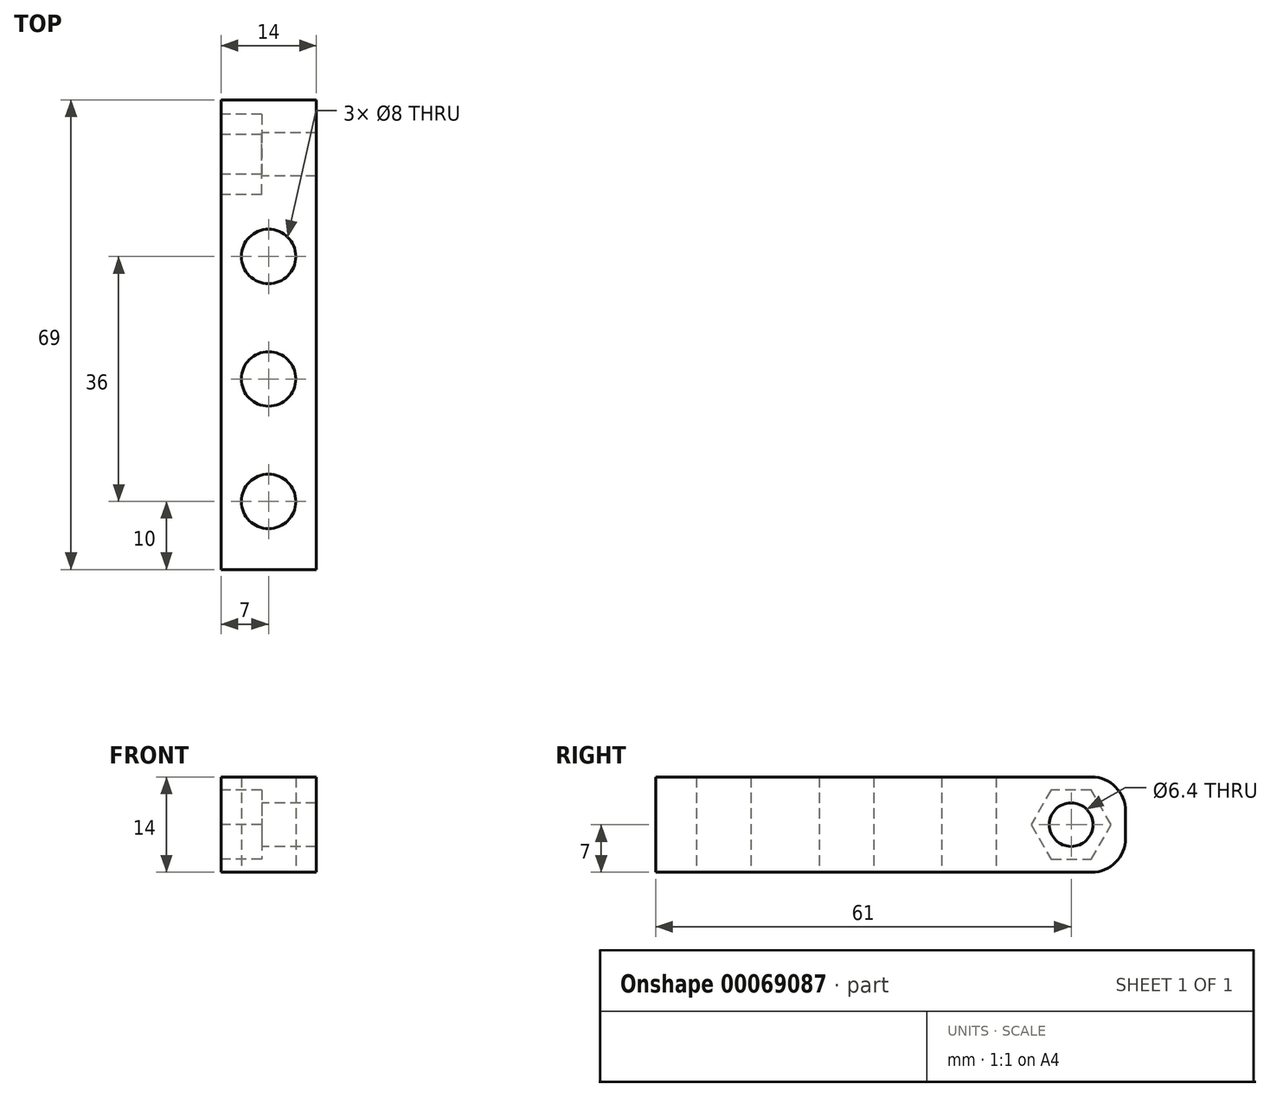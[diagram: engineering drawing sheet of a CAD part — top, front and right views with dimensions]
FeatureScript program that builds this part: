
annotation { "Feature Type Name" : "Feature", "Feature Type Description" : "" }
export const myFeature = defineFeature(function(context is Context, id is Id, definition is map)
    precondition{}
    {
        {
            var Q0;
            Q0=qCreatedBy(makeId("Top.planeOp"),FACE);
            var sketch = newSketch(context, id + "F0", { "sketchPlane" : qUnion([Q0])});
            skLineSegment(sketch, "E0", {"start": v(0, 0) * mm, "end": v(0, 69) * mm});
            skLineSegment(sketch, "E1", {"start": v(0, 69) * mm, "end": v(14, 69) * mm});
            skLineSegment(sketch, "E2", {"start": v(14, 69) * mm, "end": v(14, 0) * mm});
            skLineSegment(sketch, "E3", {"start": v(14, 0) * mm, "end": v(0, 0) * mm});
            skCircle(sketch, "E4", {"center": v(7, 10) * mm, "radius": 4 * mm});
            skLineSegment(sketch, "E5", {"start": v(0, 61) * mm, "end": v(14, 61) * mm, "construction": true});
            skPoint(sketch, "E6", {"position": v(7, 80) * mm});
            skPoint(sketch, "E6.positionSnap0", {"position": v(7, 69) * mm});
            skCircle(sketch, "E7", {"center": v(7, 28) * mm, "radius": 4 * mm});
            skCircle(sketch, "E8", {"center": v(7, 46) * mm, "radius": 4 * mm});
            skPoint(sketch, "E9", {"position": v(7, 141) * mm});
            skPoint(sketch, "E10", {"position": v(7, -19) * mm});
            skSolve(sketch);
        }
        {
            var Q0;
            Q0 = qSketchRegion(id + "F0", true);
            extrude(context, id + "F1", {"entities" : qUnion([Q0]), "depth" : 14 * mm});
        }
        {
            var Q0;
            Q0=makeQuery(id+"F1.opExtrude","SWEPT_FACE",FACE,{"disambiguationData":[OSD([sQuery(id+"F0.wireOp",EDGE,"E0")])]});
            var sketch = newSketch(context, id + "F2", { "sketchPlane" : qUnion([Q0])});
            skPoint(sketch, "E11.0", {"position": v(-61, 0) * mm});
            skCircle(sketch, "E12", {"center": v(-61, 7) * mm, "radius": 3.2 * mm});
            skPoint(sketch, "E12.centerSnap0", {"position": v(-69, 7) * mm});
            skCircle(sketch, "E13.cCircle", {"center": v(-61, 7) * mm, "radius": 5.1 * mm, "construction": true});
            skLineSegment(sketch, "E13.0", {"start": v(-58.06, 1.9) * mm, "end": v(-63.94, 1.9) * mm});
            skLineSegment(sketch, "E13.1", {"start": v(-63.94, 1.9) * mm, "end": v(-66.89, 7) * mm});
            skLineSegment(sketch, "E13.2", {"start": v(-66.89, 7) * mm, "end": v(-63.94, 12.1) * mm});
            skLineSegment(sketch, "E13.3", {"start": v(-63.94, 12.1) * mm, "end": v(-58.06, 12.1) * mm});
            skLineSegment(sketch, "E13.4", {"start": v(-58.06, 12.1) * mm, "end": v(-55.11, 7) * mm});
            skLineSegment(sketch, "E13.5", {"start": v(-55.11, 7) * mm, "end": v(-58.06, 1.9) * mm});
            skPoint(sketch, "E13.0.midPoint", {"position": v(-61, 1.9) * mm});
            skSolve(sketch);
        }
        {
            var Q0;
            Q0=makeQuery(id+"F2.imprint","IMPRINT",FACE,{"disambiguationData":[TD([[makeQuery(id+"F2.imprint","IMPRINT",EDGE,{"derivedFrom":sQuery(id+"F2.wireOp",EDGE,"E12")}),1.0]])]});
            extrude(context, id + "F3", {"entities" : qUnion([Q0]), "operationType" : NewBodyOperationType.REMOVE, "endBound" : BoundingType.THROUGH_ALL, "oppositeDirection" : true, "depth" : 25 * mm});
        }
        {
            var Q0;
            Q0=makeQuery(id+"F2.imprint","IMPRINT",FACE,{"disambiguationData":[TD([[makeQuery(id+"F2.imprint","IMPRINT",EDGE,{"derivedFrom":sQuery(id+"F2.wireOp",EDGE,"E12")}),-1.0]])]});
            extrude(context, id + "F4", {"entities" : qUnion([Q0]), "operationType" : NewBodyOperationType.REMOVE, "oppositeDirection" : true, "depth" : 6 * mm});
        }
        {
            var Q0;
            Q0=makeQuery(id+"F1.opExtrude","CAP_EDGE",EDGE,{"disambiguationData":[OSD([sQuery(id+"F0.wireOp",EDGE,"E1")])],"isStart":false});
            var Q1;
            Q1=makeQuery(id+"F1.opExtrude","CAP_EDGE",EDGE,{"disambiguationData":[OSD([sQuery(id+"F0.wireOp",EDGE,"E1")])],"isStart":true});
            fillet(context, id + "F5", {"entities" : qUnion([Q0, Q1]), "radius" : 5 * mm, "tangentPropagation" : true, "allowEdgeOverflow" : false});
        }
    });
